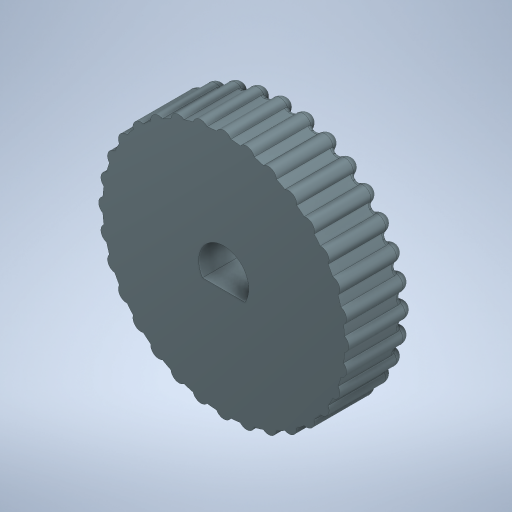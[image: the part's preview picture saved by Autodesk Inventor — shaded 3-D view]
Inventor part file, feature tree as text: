
AUTODESK INVENTOR PART (.ipt)
format: ipt  version: 2024.2 (Build 282272000, 272)  size: 1,431,552 bytes
history: native  units: mm
features: extrude x4, fillet x4, sketch x3
ambient origin geometry x8: Origin, YZ Plane, XZ Plane, XY Plane, X Axis, Y Axis, Z Axis, Center Point
bodies: Solide1 (feature_tree)
feature tree (11):
  sketch  "Esquisse1"
  extrude  "Extrusion1"  Depth=6.2mm
  extrude  "Extrusion2"  Depth=5.25mm
  extrude  "Extrusion3"  Depth=30.0mm
  fillet  "Congé1"  Radius=7.0mm
  fillet  "Congé2"  Radius=6.0mm
  fillet  "Congé3"  Radius=2.0mm
  extrude  "Extrusion4"  Depth=14.5mm
  fillet  "Congé4"  Radius=320.0mm
  sketch  "Esquisse2"
  sketch  "Esquisse3"
